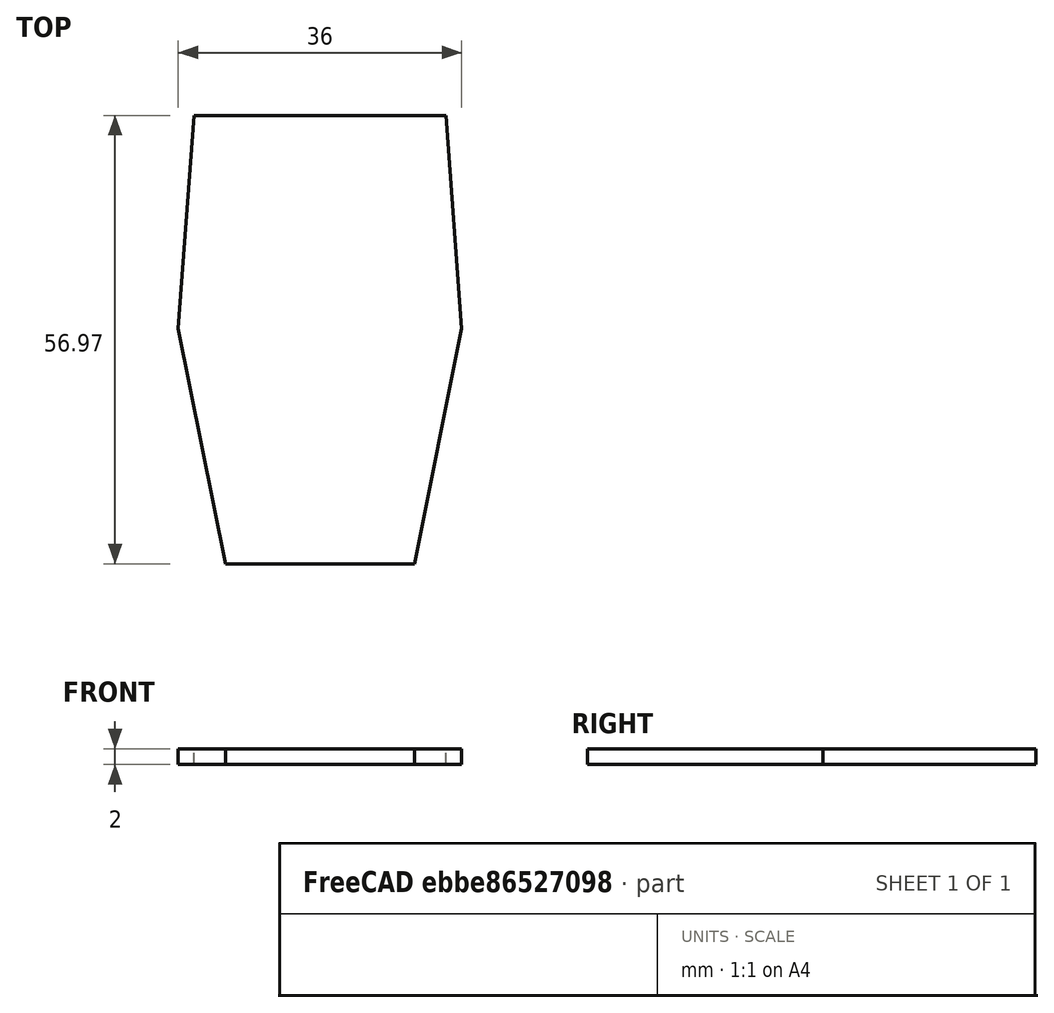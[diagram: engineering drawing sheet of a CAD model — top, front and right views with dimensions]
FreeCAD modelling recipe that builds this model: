
FCSTD DOCUMENT  (FreeCAD 0.20R29603 (Git))
Label: KeyFobBelt
License: All rights reserved
LicenseURL: http://en.wikipedia.org/wiki/All_rights_reserved
objects: Sketcher::SketchObject×1, PartDesign::Pad×1, PartDesign::Body×1, App::Part×1
note: 4 computed .brp shape members not serialized (recipe doc carries the construction recipe); baked Part::Feature solids carry a one-line shape summary decoded from their .brp

FEATURE [Sketcher::SketchObject] Sketch
  FullyConstrained = true
  MapMode = 5
  Support = -> [XY_Plane001]
  sketch-geometry (6):
    g0: LineSegment StartX=-16 StartY=27.09 StartZ=0 EndX=-18 EndY=0 EndZ=0
    g1: LineSegment StartX=-18 StartY=0 StartZ=0 EndX=-12 EndY=-29.881 EndZ=0
    g2: LineSegment StartX=-12 StartY=-29.881 StartZ=0 EndX=12 EndY=-29.881 EndZ=0
    g3: LineSegment StartX=12 StartY=-29.881 StartZ=0 EndX=18 EndY=0 EndZ=0
    g4: LineSegment StartX=18 StartY=0 StartZ=0 EndX=16 EndY=27.09 EndZ=0
    g5: LineSegment StartX=16 StartY=27.09 StartZ=0 EndX=-16 EndY=27.09 EndZ=0
  constraints (16):
    c: Coincident(g0,g1)
    c: Coincident(g1,g2)
    c: Coincident(g2,g3)
    c: Coincident(g3,g4)
    c: Coincident(g4,g5)
    c: Coincident(g5,g0)
    c: DistanceX(g0,g3) = 36
    c: DistanceX(g0,g4) = 32
    c: Symmetric(g0,g4,g-2)
    c: Horizontal(g3,g0)
    c: Symmetric(g1,g2,g-2)
    c: PointOnObject(g3,g-1)
    c: DistanceX(g2,g2) = 24
    c: DistanceY(g0,g0) = 27.09
    c: DistanceY(g2,g3) = 29.881
    c: DistanceX(g0,g-1) = 18
FEATURE [PartDesign::Pad] Pad
  Direction = (0,0,1)
  Length = 2
  Length2 = 10
  Profile = -> Sketch
  ReferenceAxis = -> Sketch [N_Axis]
  Type = 0
FEATURE [PartDesign::Body] Body
  Group = -> [Sketch,Pad]
  Origin = -> Origin001
  Tip = -> Pad
FEATURE [App::Part] Part
  Group = -> [Body]
  Origin = -> Origin
